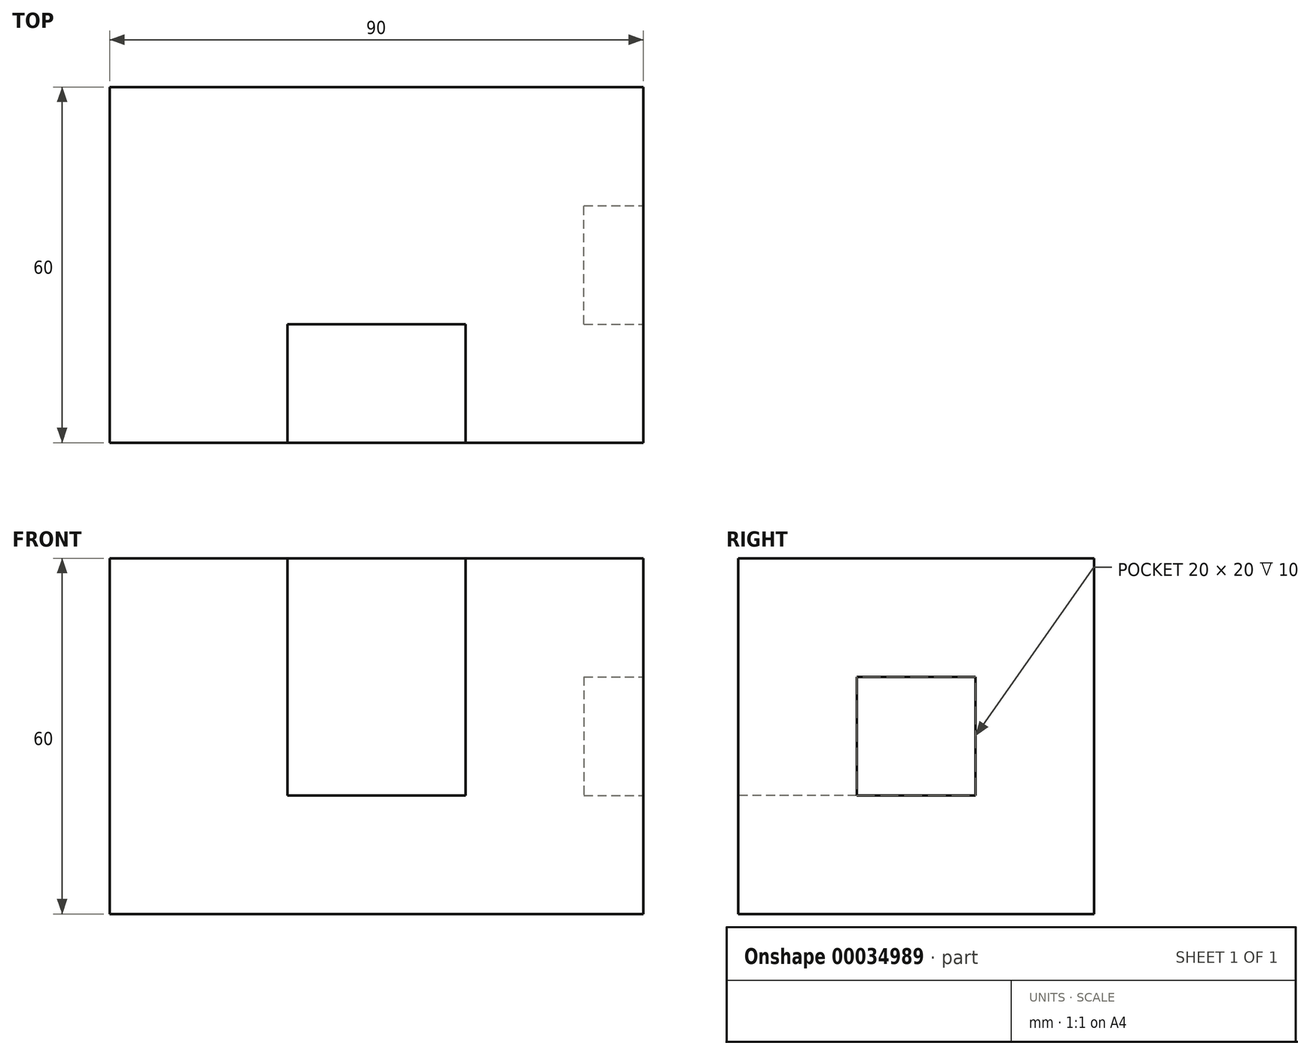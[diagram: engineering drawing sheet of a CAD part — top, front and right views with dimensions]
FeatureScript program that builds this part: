
annotation { "Feature Type Name" : "Feature", "Feature Type Description" : "" }
export const myFeature = defineFeature(function(context is Context, id is Id, definition is map)
    precondition{}
    {
        {
            var Q0;
            Q0=qCreatedBy(makeId("Front.planeOp"),FACE);
            var sketch = newSketch(context, id + "F0", { "sketchPlane" : qUnion([Q0])});
            skLineSegment(sketch, "E0.bottom", {"start": v(-47.32, 41.43) * mm, "end": v(42.68, 41.43) * mm});
            skLineSegment(sketch, "E0.top", {"start": v(-47.32, -18.57) * mm, "end": v(42.68, -18.57) * mm});
            skLineSegment(sketch, "E0.left", {"start": v(-47.32, 41.43) * mm, "end": v(-47.32, -18.57) * mm});
            skLineSegment(sketch, "E0.right", {"start": v(42.68, 41.43) * mm, "end": v(42.68, -18.57) * mm});
            skSolve(sketch);
        }
        {
            var Q0;
            Q0=makeQuery(id+"F0.imprint","IMPRINT",FACE,{"disambiguationData":[TD([[makeQuery(id+"F0.imprint","IMPRINT",EDGE,{"derivedFrom":sQuery(id+"F0.wireOp",EDGE,"E0.bottom")}),-1.0]])]});
            extrude(context, id + "F1", {"entities" : qUnion([Q0]), "depth" : 60 * mm});
        }
        {
            var Q0;
            Q0=makeQuery(id+"F1.opExtrude","CAP_FACE",FACE,{"disambiguationData":[OSD([sQuery(id+"F0.wireOp",EDGE,"E0.bottom"),sQuery(id+"F0.wireOp",EDGE,"E0.top"),sQuery(id+"F0.wireOp",EDGE,"E0.left"),sQuery(id+"F0.wireOp",EDGE,"E0.right")])],"isStart":false});
            var sketch = newSketch(context, id + "F2", { "sketchPlane" : qUnion([Q0])});
            skLineSegment(sketch, "E1.bottom", {"start": v(-17.32, 41.43) * mm, "end": v(12.68, 41.43) * mm});
            skLineSegment(sketch, "E1.top", {"start": v(-17.32, 1.43) * mm, "end": v(12.68, 1.43) * mm});
            skLineSegment(sketch, "E1.left", {"start": v(-17.32, 41.43) * mm, "end": v(-17.32, 1.43) * mm});
            skLineSegment(sketch, "E1.right", {"start": v(12.68, 41.43) * mm, "end": v(12.68, 1.43) * mm});
            skSolve(sketch);
        }
        {
            var Q0;
            Q0=makeQuery(id+"F2.imprint","IMPRINT",FACE,{"disambiguationData":[TD([[makeQuery(id+"F2.imprint","IMPRINT",EDGE,{"derivedFrom":sQuery(id+"F2.wireOp",EDGE,"E1.bottom")}),-1.0]])]});
            extrude(context, id + "F3", {"entities" : qUnion([Q0]), "operationType" : NewBodyOperationType.REMOVE, "oppositeDirection" : true, "depth" : 20 * mm});
        }
        {
            var Q0;
            Q0=makeQuery(id+"F1.opExtrude","SWEPT_FACE",FACE,{"disambiguationData":[OSD([sQuery(id+"F0.wireOp",EDGE,"E0.right")])]});
            var sketch = newSketch(context, id + "F4", { "sketchPlane" : qUnion([Q0])});
            skLineSegment(sketch, "E2.bottom", {"start": v(-40, 21.43) * mm, "end": v(-20, 21.43) * mm});
            skLineSegment(sketch, "E2.top", {"start": v(-40, 1.43) * mm, "end": v(-20, 1.43) * mm});
            skLineSegment(sketch, "E2.left", {"start": v(-40, 21.43) * mm, "end": v(-40, 1.43) * mm});
            skLineSegment(sketch, "E2.right", {"start": v(-20, 21.43) * mm, "end": v(-20, 1.43) * mm});
            skSolve(sketch);
        }
        {
            var Q0;
            Q0=makeQuery(id+"F4.imprint","IMPRINT",FACE,{"disambiguationData":[TD([[makeQuery(id+"F4.imprint","IMPRINT",EDGE,{"derivedFrom":sQuery(id+"F4.wireOp",EDGE,"E2.bottom")}),-1.0]])]});
            var Q1;
            Q1=makeQuery(id+"F3.boolean.opBoolean","COPY",FACE,{"derivedFrom":makeQuery(id+"F3.opExtrude","SWEPT_FACE",FACE,{"disambiguationData":[OSD([sQuery(id+"F2.wireOp",EDGE,"E1.right")])]})});
            extrude(context, id + "F5", {"entities" : qUnion([Q0]), "operationType" : NewBodyOperationType.REMOVE, "oppositeDirection" : true, "endBoundEntityFace" : qUnion([Q1]), "depth" : 10 * mm});
        }
    });
